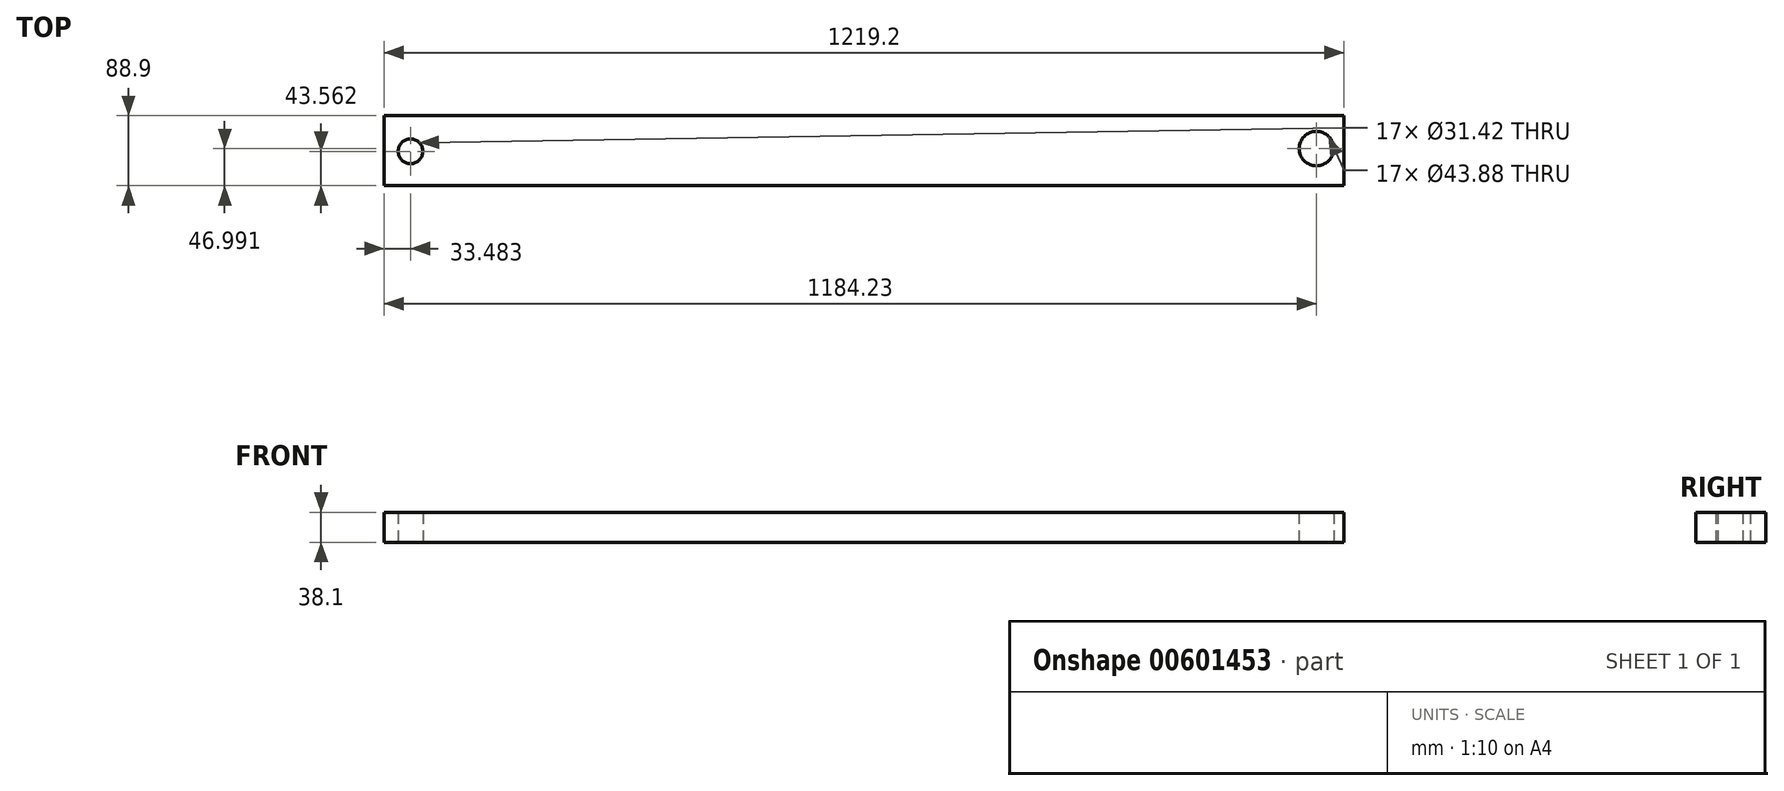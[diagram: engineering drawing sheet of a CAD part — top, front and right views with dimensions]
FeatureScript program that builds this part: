
annotation { "Feature Type Name" : "Feature", "Feature Type Description" : "" }
export const myFeature = defineFeature(function(context is Context, id is Id, definition is map)
    precondition{}
    {
        {
            var Q0;
            Q0=qCreatedBy(makeId("Top.planeOp"),FACE);
            var sketch = newSketch(context, id + "F0", { "sketchPlane" : qUnion([Q0])});
            skLineSegment(sketch, "E0.bottom", {"start": v(0, 0) * mm, "end": v(1219.2, 0) * mm});
            skLineSegment(sketch, "E0.top", {"start": v(0, 88.9) * mm, "end": v(1219.2, 88.9) * mm});
            skLineSegment(sketch, "E0.left", {"start": v(0, 0) * mm, "end": v(0, 88.9) * mm});
            skLineSegment(sketch, "E0.right", {"start": v(1219.2, 0) * mm, "end": v(1219.2, 88.9) * mm});
            skCircle(sketch, "E1", {"center": v(33.48, 43.56) * mm, "radius": 15.7 * mm});
            skCircle(sketch, "E2", {"center": v(1184.23, 47) * mm, "radius": 21.94 * mm});
            skSolve(sketch);
        }
        {
            var Q0;
            Q0=qSketchRegion(id+"F0",true);
            extrude(context, id + "F1", {"entities" : qUnion([Q0]), "depth" : 38.1 * mm, "offsetDistance" : 25.4 * mm});
        }
    });
